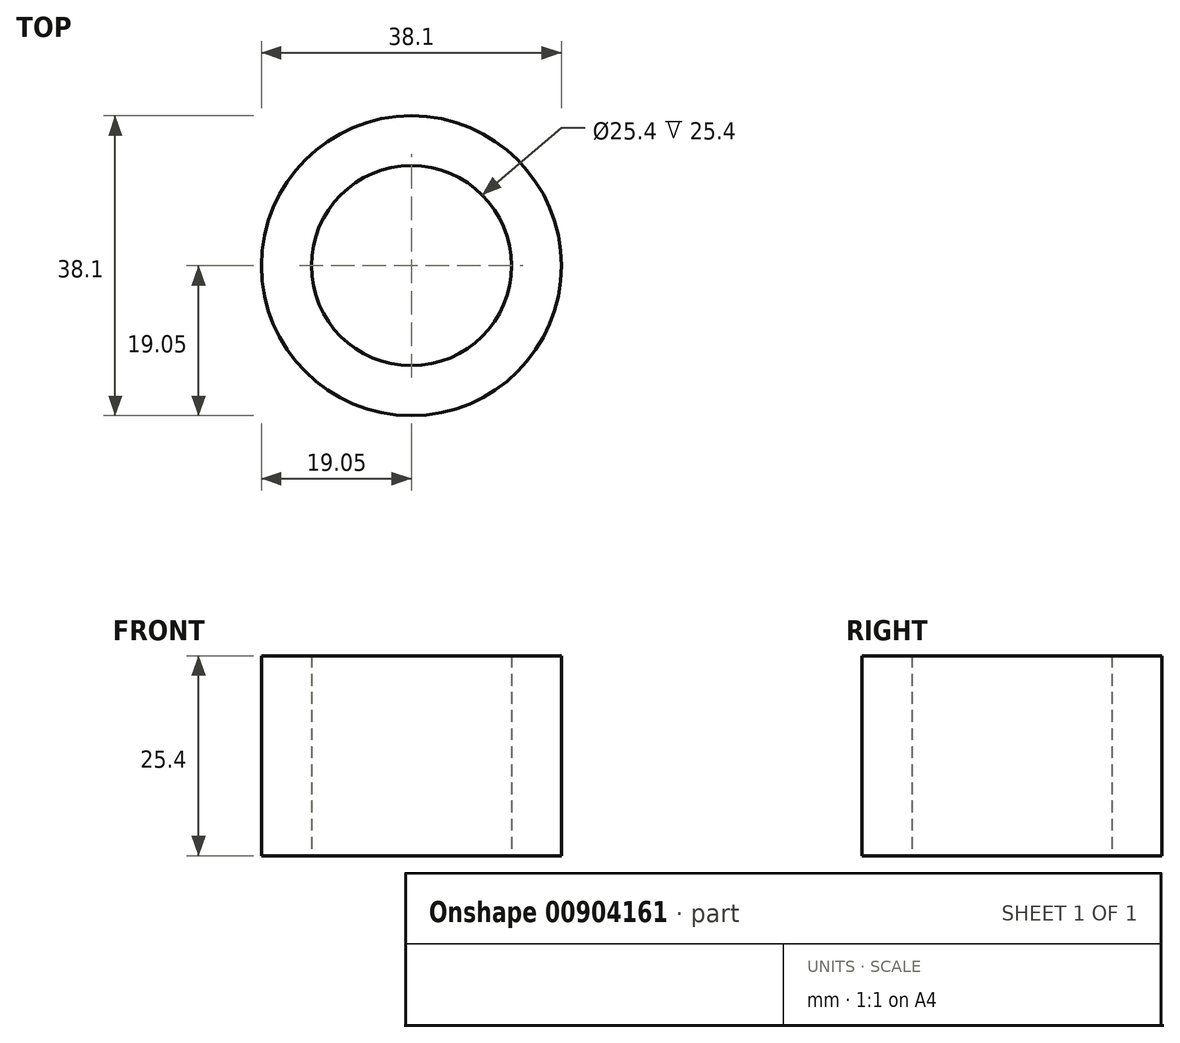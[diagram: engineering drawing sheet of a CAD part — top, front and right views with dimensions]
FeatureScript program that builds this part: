
annotation { "Feature Type Name" : "Feature", "Feature Type Description" : "" }
export const myFeature = defineFeature(function(context is Context, id is Id, definition is map)
    precondition{}
    {
        {
            var Q0;
            Q0=qCreatedBy(makeId("Top.planeOp"),FACE);
            var sketch = newSketch(context, id + "F0", { "sketchPlane" : qUnion([Q0])});
            skCircle(sketch, "E0", {"center": v(0, 0) * mm, "radius": 12.7 * mm});
            skCircle(sketch, "E1", {"center": v(0, 0) * mm, "radius": 19.05 * mm});
            skSolve(sketch);
        }
        {
            var Q0;
            Q0 = qSketchRegion(id + "F0", true);
            var Q1;
            Q1=sQuery(id+"F0.wireOp",EDGE,"E0");
            var Q2;
            Q2=sQuery(id+"F0.wireOp",EDGE,"E1");
            extrude(context, id + "F1", {"entities" : qUnion([Q0]), "surfaceEntities" : qUnion([Q1, Q2]), "depth" : 25.4 * mm, "offsetDistance" : 25.4 * mm});
        }
    });
